# Revit family: EuroTambours_Single
name_source: partatom
category: Furniture
revit_build: Autodesk Revit 2016 (Build: 20150714_1515(x64)
units: mm (PartAtom-declared; Revit-internal decimal feet)

## family parameters
Always vertical = Yes
Cut with Voids When Loaded = No
OmniClass Number = 23.40.20.00
OmniClass Title = General Furniture and Specialties
Room Calculation Point = No
Shared = No
Work Plane-Based = No

## types (7) — shared parameters
Depth = 430 mm
Tambour array = 24
Width = 800 mm  [stored 2.62467 ft]

## per-type parameters (varying)
| type | Doors height | Height | Lock bar height | Plinth height | plinth start height |
| ET408/TB | 391 mm  [stored 1.28281 ft] | 495 mm  [stored 1.62402 ft] | 386 mm | 55 mm  [stored 0.180446 ft] | 386 mm |
| ET408/06 | 561 mm | 695 mm  [stored 2.28018 ft] | 556 mm | 85 mm  [stored 0.278871 ft] | -5 mm  [stored -0.0164042 ft] |
| ET408/10 | 896 mm  [stored 2.93963 ft] | 1030 mm  [stored 3.37927 ft] | 891 mm | 85 mm  [stored 0.278871 ft] | -5 mm  [stored -0.0164042 ft] |
| ET408/11 | 1047 mm | 1181 mm  [stored 3.87467 ft] | 1042 mm | 85 mm  [stored 0.278871 ft] | -5 mm  [stored -0.0164042 ft] |
| ET408/13 | 1196 mm | 1330 mm  [stored 4.36352 ft] | 1191 mm | 85 mm  [stored 0.278871 ft] | -5 mm  [stored -0.0164042 ft] |
| ET408/17 | 1503 mm  [stored 4.9311 ft] | 1637 mm  [stored 5.37073 ft] | 1498 mm  [stored 4.9147 ft] | 85 mm  [stored 0.278871 ft] | -5 mm  [stored -0.0164042 ft] |
| ET408/19 | 1846 mm  [stored 6.05643 ft] | 1980 mm  [stored 6.49606 ft] | 1841 mm  [stored 6.04003 ft] | 85 mm  [stored 0.278871 ft] | -5 mm  [stored -0.0164042 ft] |

note: [stored X ft] marks values corroborated as IEEE doubles in the binary element streams (Revit-internal decimal feet)

## geometry (parser evidence)
native form markers: Sweep x2
no freeform markers — native parametric forms only
